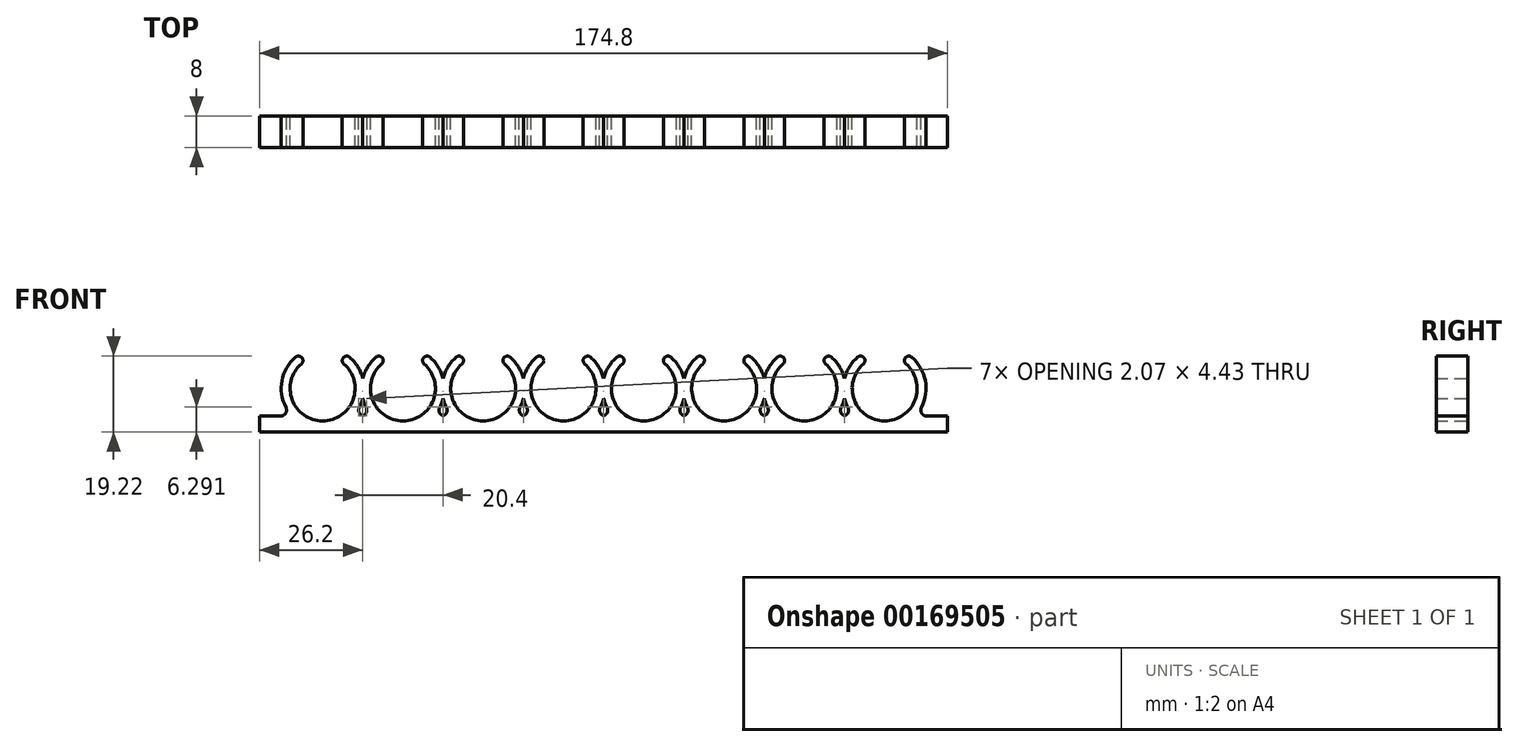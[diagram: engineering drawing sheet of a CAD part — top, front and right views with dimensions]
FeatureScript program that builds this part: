
annotation { "Feature Type Name" : "Feature", "Feature Type Description" : "" }
export const myFeature = defineFeature(function(context is Context, id is Id, definition is map)
    precondition{}
    {
        {
            var Q0;
            Q0=qCreatedBy(makeId("Front.planeOp"),FACE);
            var sketch = newSketch(context, id + "F0", { "sketchPlane" : qUnion([Q0])});
            skLineSegment(sketch, "E0.bottom", {"start": v(0, 0) * mm, "end": v(32, 0) * mm});
            skLineSegment(sketch, "E0.top", {"start": v(0, 4) * mm, "end": v(5.33, 4) * mm});
            skLineSegment(sketch, "E0.left", {"start": v(0, 0) * mm, "end": v(0, 4) * mm});
            skLineSegment(sketch, "E0.right", {"start": v(32, 0) * mm, "end": v(32, 4) * mm});
            skLineSegment(sketch, "E1", {"start": v(16, 16.58) * mm, "end": v(16, -10.01) * mm, "construction": true});
            skLineSegment(sketch, "E2", {"start": v(-9.88, 11) * mm, "end": v(205.8, 11) * mm, "construction": true});
            skArc(sketch, "E3", {"start": v(10.61, 17.25) * mm, "mid": v(16, 2.75) * mm, "end": v(21.39, 17.25) * mm});
            skArc(sketch, "E4", {"start": v(9.14, 18.95) * mm, "mid": v(5.7, 13) * mm, "end": v(6.67, 6.19) * mm});
            skArc(sketch, "E5", {"start": v(10.6, 17.25) * mm, "mid": v(10.73, 18.83) * mm, "end": v(9.14, 18.95) * mm});
            skArc(sketch, "E6.MirrorC", {"start": v(21.4, 17.25) * mm, "mid": v(21.27, 18.83) * mm, "end": v(22.86, 18.95) * mm});
            skArc(sketch, "E7", {"start": v(5.33, 4) * mm, "mid": v(6.62, 4.72) * mm, "end": v(6.67, 6.19) * mm});
            skArc(sketch, "E8.MirrorC", {"start": v(26.67, 4) * mm, "mid": v(25.38, 4.72) * mm, "end": v(25.33, 6.19) * mm});
            skLineSegment(sketch, "E9.trimOffspring", {"start": v(26.67, 4) * mm, "end": v(32, 4) * mm});
            skArc(sketch, "E10.trimOffspring", {"start": v(25.33, 6.19) * mm, "mid": v(26.3, 13) * mm, "end": v(22.86, 18.95) * mm});
            skLineSegment(sketch, "E11.direction1", {"start": v(0, 0) * mm, "end": v(32, 0) * mm, "construction": true});
            skArc(sketch, "E12.1.0.0", {"start": v(45.73, 6.19) * mm, "mid": v(46.7, 13) * mm, "end": v(43.26, 18.95) * mm});
            skLineSegment(sketch, "E12.1.0.1", {"start": v(20.4, 0) * mm, "end": v(52.4, 0) * mm, "construction": true});
            skLineSegment(sketch, "E12.1.0.2", {"start": v(20.4, 4) * mm, "end": v(25.73, 4) * mm});
            skLineSegment(sketch, "E12.1.0.3", {"start": v(20.4, 0) * mm, "end": v(20.4, 4) * mm});
            skLineSegment(sketch, "E12.1.0.4", {"start": v(52.4, 0) * mm, "end": v(52.4, 4) * mm});
            skArc(sketch, "E12.1.0.5", {"start": v(31.01, 17.25) * mm, "mid": v(36.4, 2.75) * mm, "end": v(41.79, 17.25) * mm});
            skArc(sketch, "E12.1.0.6", {"start": v(29.54, 18.95) * mm, "mid": v(26.1, 13) * mm, "end": v(27.07, 6.19) * mm});
            skArc(sketch, "E12.1.0.7", {"start": v(47.07, 4) * mm, "mid": v(45.78, 4.72) * mm, "end": v(45.73, 6.19) * mm});
            skLineSegment(sketch, "E12.1.0.8", {"start": v(47.07, 4) * mm, "end": v(52.4, 4) * mm});
            skLineSegment(sketch, "E12.1.0.9", {"start": v(20.4, 0) * mm, "end": v(52.4, 0) * mm});
            skArc(sketch, "E12.1.0.10", {"start": v(31, 17.25) * mm, "mid": v(31.13, 18.83) * mm, "end": v(29.54, 18.95) * mm});
            skArc(sketch, "E12.1.0.11", {"start": v(41.8, 17.25) * mm, "mid": v(41.67, 18.83) * mm, "end": v(43.26, 18.95) * mm});
            skArc(sketch, "E12.1.0.12", {"start": v(25.73, 4) * mm, "mid": v(27.02, 4.72) * mm, "end": v(27.07, 6.19) * mm});
            skArc(sketch, "E12.2.0.0", {"start": v(66.13, 6.19) * mm, "mid": v(67.1, 13) * mm, "end": v(63.66, 18.95) * mm});
            skLineSegment(sketch, "E12.2.0.1", {"start": v(40.8, 0) * mm, "end": v(72.8, 0) * mm, "construction": true});
            skLineSegment(sketch, "E12.2.0.2", {"start": v(40.8, 4) * mm, "end": v(46.13, 4) * mm});
            skLineSegment(sketch, "E12.2.0.3", {"start": v(40.8, 0) * mm, "end": v(40.8, 4) * mm});
            skLineSegment(sketch, "E12.2.0.4", {"start": v(72.8, 0) * mm, "end": v(72.8, 4) * mm});
            skArc(sketch, "E12.2.0.5", {"start": v(51.41, 17.25) * mm, "mid": v(56.8, 2.75) * mm, "end": v(62.19, 17.25) * mm});
            skArc(sketch, "E12.2.0.6", {"start": v(49.94, 18.95) * mm, "mid": v(46.5, 13) * mm, "end": v(47.47, 6.19) * mm});
            skArc(sketch, "E12.2.0.7", {"start": v(67.47, 4) * mm, "mid": v(66.18, 4.72) * mm, "end": v(66.13, 6.19) * mm});
            skLineSegment(sketch, "E12.2.0.8", {"start": v(67.47, 4) * mm, "end": v(72.8, 4) * mm});
            skLineSegment(sketch, "E12.2.0.9", {"start": v(40.8, 0) * mm, "end": v(72.8, 0) * mm});
            skArc(sketch, "E12.2.0.10", {"start": v(51.4, 17.25) * mm, "mid": v(51.53, 18.83) * mm, "end": v(49.94, 18.95) * mm});
            skArc(sketch, "E12.2.0.11", {"start": v(62.2, 17.25) * mm, "mid": v(62.07, 18.83) * mm, "end": v(63.66, 18.95) * mm});
            skArc(sketch, "E12.2.0.12", {"start": v(46.13, 4) * mm, "mid": v(47.42, 4.72) * mm, "end": v(47.47, 6.19) * mm});
            skArc(sketch, "E12.3.0.0", {"start": v(86.53, 6.19) * mm, "mid": v(87.5, 13) * mm, "end": v(84.06, 18.95) * mm});
            skLineSegment(sketch, "E12.3.0.1", {"start": v(61.2, 0) * mm, "end": v(93.2, 0) * mm, "construction": true});
            skLineSegment(sketch, "E12.3.0.2", {"start": v(61.2, 4) * mm, "end": v(66.53, 4) * mm});
            skLineSegment(sketch, "E12.3.0.3", {"start": v(61.2, 0) * mm, "end": v(61.2, 4) * mm});
            skLineSegment(sketch, "E12.3.0.4", {"start": v(93.2, 0) * mm, "end": v(93.2, 4) * mm});
            skArc(sketch, "E12.3.0.5", {"start": v(71.81, 17.25) * mm, "mid": v(77.2, 2.75) * mm, "end": v(82.6, 17.25) * mm});
            skArc(sketch, "E12.3.0.6", {"start": v(70.34, 18.95) * mm, "mid": v(66.9, 13) * mm, "end": v(67.87, 6.19) * mm});
            skArc(sketch, "E12.3.0.7", {"start": v(87.87, 4) * mm, "mid": v(86.58, 4.72) * mm, "end": v(86.53, 6.19) * mm});
            skLineSegment(sketch, "E12.3.0.8", {"start": v(87.87, 4) * mm, "end": v(93.2, 4) * mm});
            skLineSegment(sketch, "E12.3.0.9", {"start": v(61.2, 0) * mm, "end": v(93.2, 0) * mm});
            skArc(sketch, "E12.3.0.10", {"start": v(71.81, 17.25) * mm, "mid": v(71.93, 18.83) * mm, "end": v(70.34, 18.95) * mm});
            skArc(sketch, "E12.3.0.11", {"start": v(82.6, 17.25) * mm, "mid": v(82.47, 18.83) * mm, "end": v(84.06, 18.95) * mm});
            skArc(sketch, "E12.3.0.12", {"start": v(66.53, 4) * mm, "mid": v(67.82, 4.72) * mm, "end": v(67.87, 6.19) * mm});
            skArc(sketch, "E12.4.0.0", {"start": v(106.93, 6.19) * mm, "mid": v(107.9, 13) * mm, "end": v(104.46, 18.95) * mm});
            skLineSegment(sketch, "E12.4.0.1", {"start": v(81.6, 0) * mm, "end": v(113.6, 0) * mm, "construction": true});
            skLineSegment(sketch, "E12.4.0.2", {"start": v(81.6, 4) * mm, "end": v(86.93, 4) * mm});
            skLineSegment(sketch, "E12.4.0.3", {"start": v(81.6, 0) * mm, "end": v(81.6, 4) * mm});
            skLineSegment(sketch, "E12.4.0.4", {"start": v(113.6, 0) * mm, "end": v(113.6, 4) * mm});
            skArc(sketch, "E12.4.0.5", {"start": v(92.21, 17.25) * mm, "mid": v(97.6, 2.75) * mm, "end": v(102.99, 17.25) * mm});
            skArc(sketch, "E12.4.0.6", {"start": v(90.74, 18.95) * mm, "mid": v(87.3, 13) * mm, "end": v(88.27, 6.19) * mm});
            skArc(sketch, "E12.4.0.7", {"start": v(108.27, 4) * mm, "mid": v(106.98, 4.72) * mm, "end": v(106.93, 6.19) * mm});
            skLineSegment(sketch, "E12.4.0.8", {"start": v(108.27, 4) * mm, "end": v(113.6, 4) * mm});
            skLineSegment(sketch, "E12.4.0.9", {"start": v(81.6, 0) * mm, "end": v(113.6, 0) * mm});
            skArc(sketch, "E12.4.0.10", {"start": v(92.2, 17.25) * mm, "mid": v(92.33, 18.83) * mm, "end": v(90.74, 18.95) * mm});
            skArc(sketch, "E12.4.0.11", {"start": v(102.99, 17.25) * mm, "mid": v(102.87, 18.83) * mm, "end": v(104.46, 18.95) * mm});
            skArc(sketch, "E12.4.0.12", {"start": v(86.93, 4) * mm, "mid": v(88.22, 4.72) * mm, "end": v(88.27, 6.19) * mm});
            skArc(sketch, "E12.5.0.0", {"start": v(127.33, 6.19) * mm, "mid": v(128.3, 13) * mm, "end": v(124.86, 18.95) * mm});
            skLineSegment(sketch, "E12.5.0.1", {"start": v(102, 0) * mm, "end": v(134, 0) * mm, "construction": true});
            skLineSegment(sketch, "E12.5.0.2", {"start": v(102, 4) * mm, "end": v(107.33, 4) * mm});
            skLineSegment(sketch, "E12.5.0.3", {"start": v(102, 0) * mm, "end": v(102, 4) * mm});
            skLineSegment(sketch, "E12.5.0.4", {"start": v(134, 0) * mm, "end": v(134, 4) * mm});
            skArc(sketch, "E12.5.0.5", {"start": v(112.61, 17.25) * mm, "mid": v(118, 2.75) * mm, "end": v(123.39, 17.25) * mm});
            skArc(sketch, "E12.5.0.6", {"start": v(111.14, 18.95) * mm, "mid": v(107.7, 13) * mm, "end": v(108.67, 6.19) * mm});
            skArc(sketch, "E12.5.0.7", {"start": v(128.67, 4) * mm, "mid": v(127.38, 4.72) * mm, "end": v(127.33, 6.19) * mm});
            skLineSegment(sketch, "E12.5.0.8", {"start": v(128.67, 4) * mm, "end": v(134, 4) * mm});
            skLineSegment(sketch, "E12.5.0.9", {"start": v(102, 0) * mm, "end": v(134, 0) * mm});
            skArc(sketch, "E12.5.0.10", {"start": v(112.61, 17.25) * mm, "mid": v(112.73, 18.83) * mm, "end": v(111.14, 18.95) * mm});
            skArc(sketch, "E12.5.0.11", {"start": v(123.39, 17.25) * mm, "mid": v(123.27, 18.83) * mm, "end": v(124.86, 18.95) * mm});
            skArc(sketch, "E12.5.0.12", {"start": v(107.33, 4) * mm, "mid": v(108.62, 4.72) * mm, "end": v(108.67, 6.19) * mm});
            skArc(sketch, "E12.6.0.0", {"start": v(147.73, 6.19) * mm, "mid": v(148.7, 13) * mm, "end": v(145.26, 18.95) * mm});
            skLineSegment(sketch, "E12.6.0.1", {"start": v(122.4, 0) * mm, "end": v(154.4, 0) * mm, "construction": true});
            skLineSegment(sketch, "E12.6.0.2", {"start": v(122.4, 4) * mm, "end": v(127.73, 4) * mm});
            skLineSegment(sketch, "E12.6.0.3", {"start": v(122.4, 0) * mm, "end": v(122.4, 4) * mm});
            skLineSegment(sketch, "E12.6.0.4", {"start": v(154.4, 0) * mm, "end": v(154.4, 4) * mm});
            skArc(sketch, "E12.6.0.5", {"start": v(133.01, 17.25) * mm, "mid": v(138.4, 2.75) * mm, "end": v(143.79, 17.25) * mm});
            skArc(sketch, "E12.6.0.6", {"start": v(131.54, 18.95) * mm, "mid": v(128.1, 13) * mm, "end": v(129.07, 6.19) * mm});
            skArc(sketch, "E12.6.0.7", {"start": v(149.07, 4) * mm, "mid": v(147.78, 4.72) * mm, "end": v(147.73, 6.19) * mm});
            skLineSegment(sketch, "E12.6.0.8", {"start": v(149.07, 4) * mm, "end": v(154.4, 4) * mm});
            skLineSegment(sketch, "E12.6.0.9", {"start": v(122.4, 0) * mm, "end": v(154.4, 0) * mm});
            skArc(sketch, "E12.6.0.10", {"start": v(133, 17.25) * mm, "mid": v(133.13, 18.83) * mm, "end": v(131.54, 18.95) * mm});
            skArc(sketch, "E12.6.0.11", {"start": v(143.8, 17.25) * mm, "mid": v(143.67, 18.83) * mm, "end": v(145.26, 18.95) * mm});
            skArc(sketch, "E12.6.0.12", {"start": v(127.73, 4) * mm, "mid": v(129.02, 4.72) * mm, "end": v(129.07, 6.19) * mm});
            skArc(sketch, "E12.7.0.0", {"start": v(168.13, 6.19) * mm, "mid": v(169.1, 13) * mm, "end": v(165.66, 18.95) * mm});
            skLineSegment(sketch, "E12.7.0.1", {"start": v(142.8, 0) * mm, "end": v(174.8, 0) * mm, "construction": true});
            skLineSegment(sketch, "E12.7.0.2", {"start": v(142.8, 4) * mm, "end": v(148.13, 4) * mm});
            skLineSegment(sketch, "E12.7.0.3", {"start": v(142.8, 0) * mm, "end": v(142.8, 4) * mm});
            skLineSegment(sketch, "E12.7.0.4", {"start": v(174.8, 0) * mm, "end": v(174.8, 4) * mm});
            skArc(sketch, "E12.7.0.5", {"start": v(153.41, 17.25) * mm, "mid": v(158.8, 2.75) * mm, "end": v(164.19, 17.25) * mm});
            skArc(sketch, "E12.7.0.6", {"start": v(151.94, 18.95) * mm, "mid": v(148.5, 13) * mm, "end": v(149.47, 6.19) * mm});
            skArc(sketch, "E12.7.0.7", {"start": v(169.47, 4) * mm, "mid": v(168.18, 4.72) * mm, "end": v(168.13, 6.19) * mm});
            skLineSegment(sketch, "E12.7.0.8", {"start": v(169.47, 4) * mm, "end": v(174.8, 4) * mm});
            skLineSegment(sketch, "E12.7.0.9", {"start": v(142.8, 0) * mm, "end": v(174.8, 0) * mm});
            skArc(sketch, "E12.7.0.10", {"start": v(153.4, 17.25) * mm, "mid": v(153.53, 18.83) * mm, "end": v(151.94, 18.95) * mm});
            skArc(sketch, "E12.7.0.11", {"start": v(164.2, 17.25) * mm, "mid": v(164.07, 18.83) * mm, "end": v(165.66, 18.95) * mm});
            skArc(sketch, "E12.7.0.12", {"start": v(148.13, 4) * mm, "mid": v(149.42, 4.72) * mm, "end": v(149.47, 6.19) * mm});
            skLineSegment(sketch, "E12.direction1", {"start": v(0, 0) * mm, "end": v(20.4, 0) * mm, "construction": true});
            skSolve(sketch);
        }
        {
            var Q0;
            Q0 = qSketchRegion(id + "F0", true);
            extrude(context, id + "F1", {"entities" : qUnion([Q0]), "depth" : 8 * mm});
        }
    });
